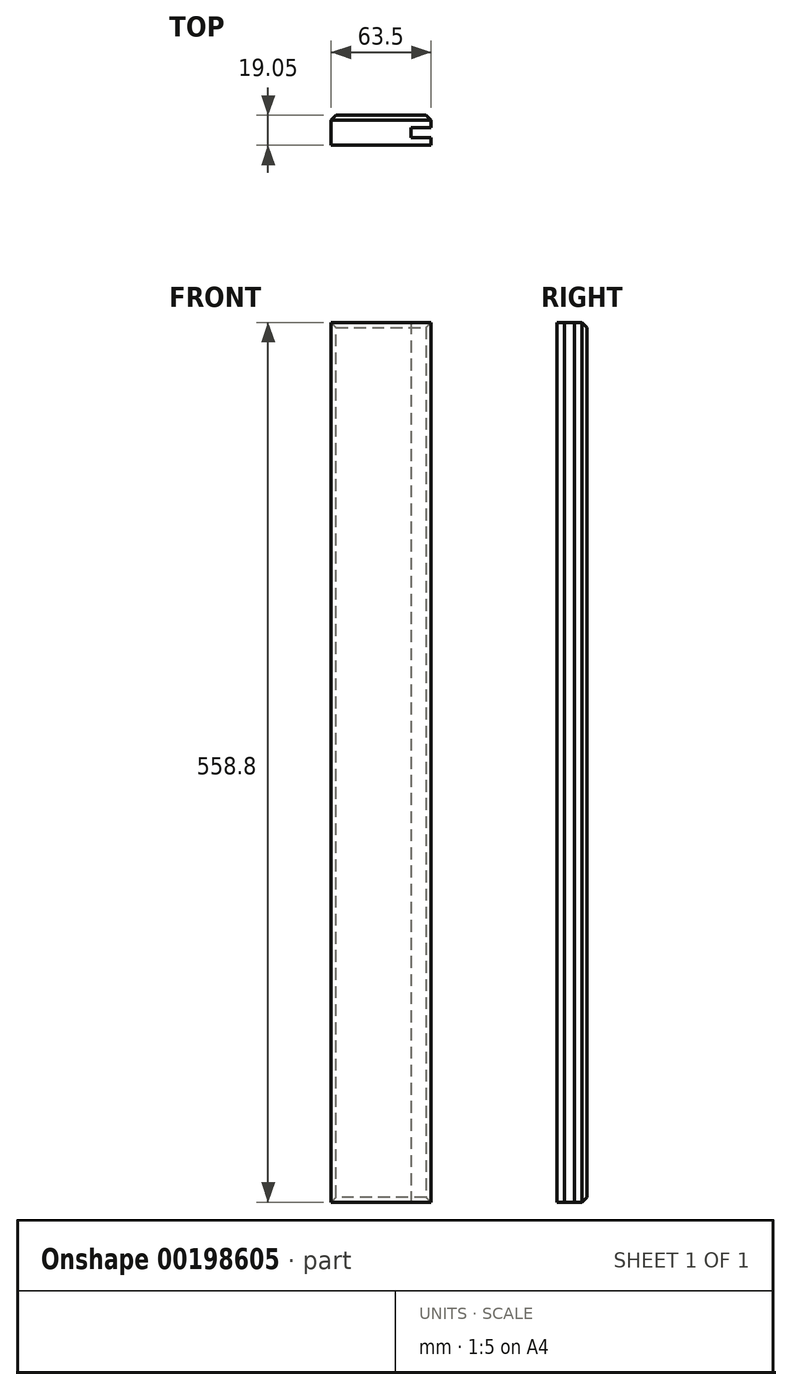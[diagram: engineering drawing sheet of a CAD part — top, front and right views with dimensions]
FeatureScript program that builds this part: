
annotation { "Feature Type Name" : "Feature", "Feature Type Description" : "" }
export const myFeature = defineFeature(function(context is Context, id is Id, definition is map)
    precondition{}
    {
        {
            var Q0;
            Q0=qCreatedBy(makeId("Top.planeOp"),FACE);
            var sketch = newSketch(context, id + "F0", { "sketchPlane" : qUnion([Q0])});
            skLineSegment(sketch, "E0.bottom", {"start": v(0, 0) * mm, "end": v(63.5, 0) * mm});
            skLineSegment(sketch, "E0.top", {"start": v(0, 19.05) * mm, "end": v(63.5, 19.05) * mm});
            skLineSegment(sketch, "E0.left", {"start": v(0, 0) * mm, "end": v(0, 19.05) * mm});
            skLineSegment(sketch, "E0.right", {"start": v(63.5, 0) * mm, "end": v(63.5, 19.05) * mm});
            skSolve(sketch);
        }
        {
            var Q0;
            Q0 = qSketchRegion(id + "F0", true);
            extrude(context, id + "F1", {"entities" : qUnion([Q0]), "depth" : 558.8 * mm});
        }
        {
            var Q0;
            Q0=makeQuery(id+"F1.opExtrude","SWEPT_EDGE",EDGE,{"disambiguationData":[OSD([sQuery(id+"F0.wireOp",EDGE,"E0.top"),sQuery(id+"F0.wireOp",EDGE,"E0.left")])]});
            var Q1;
            Q1=makeQuery(id+"F1.opExtrude","SWEPT_EDGE",EDGE,{"disambiguationData":[OSD([sQuery(id+"F0.wireOp",EDGE,"E0.top"),sQuery(id+"F0.wireOp",EDGE,"E0.right")])]});
            var Q2;
            Q2=makeQuery(id+"F1.opExtrude","CAP_EDGE",EDGE,{"disambiguationData":[OSD([sQuery(id+"F0.wireOp",EDGE,"E0.top")])],"isStart":true});
            var Q3;
            Q3=makeQuery(id+"F1.opExtrude","CAP_EDGE",EDGE,{"disambiguationData":[OSD([sQuery(id+"F0.wireOp",EDGE,"E0.top")])],"isStart":false});
            chamfer(context, id + "F2", {"entities" : qUnion([Q0, Q1, Q2, Q3]), "width" : 3.17 * mm, "tangentPropagation" : true});
        }
        {
            var Q0;
            Q0=makeQuery(id+"F1.opExtrude","CAP_FACE",FACE,{"disambiguationData":[OSD([sQuery(id+"F0.wireOp",EDGE,"E0.bottom"),sQuery(id+"F0.wireOp",EDGE,"E0.top"),sQuery(id+"F0.wireOp",EDGE,"E0.left"),sQuery(id+"F0.wireOp",EDGE,"E0.right")])],"isStart":true});
            var sketch = newSketch(context, id + "F3", { "sketchPlane" : qUnion([Q0])});
            skLineSegment(sketch, "E1", {"start": v(63.5, -4.76) * mm, "end": v(50.8, -4.76) * mm});
            skLineSegment(sketch, "E2", {"start": v(50.8, -4.76) * mm, "end": v(50.8, -11.11) * mm});
            skLineSegment(sketch, "E3", {"start": v(50.8, -11.11) * mm, "end": v(63.5, -11.11) * mm});
            skLineSegment(sketch, "E4", {"start": v(63.5, -11.11) * mm, "end": v(63.5, -4.76) * mm});
            skPoint(sketch, "E5.endSnap0", {"position": v(57.15, -4.76) * mm});
            skSolve(sketch);
        }
        {
            var Q0;
            Q0 = qSketchRegion(id + "F3", true);
            extrude(context, id + "F4", {"entities" : qUnion([Q0]), "operationType" : NewBodyOperationType.REMOVE, "endBound" : BoundingType.THROUGH_ALL, "oppositeDirection" : true, "depth" : 25.4 * mm});
        }
    });
